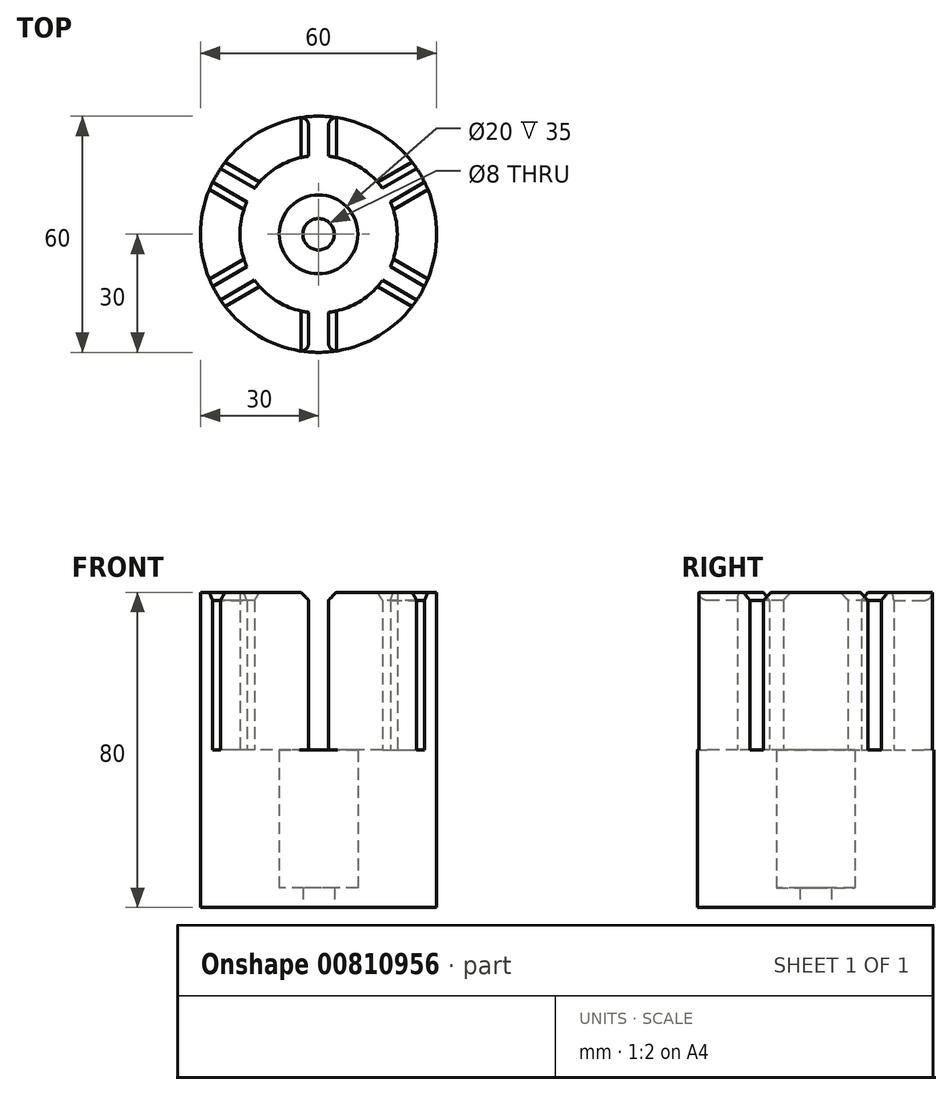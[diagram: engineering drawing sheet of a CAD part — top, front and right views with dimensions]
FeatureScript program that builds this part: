
annotation { "Feature Type Name" : "Feature", "Feature Type Description" : "" }
export const myFeature = defineFeature(function(context is Context, id is Id, definition is map)
    precondition{}
    {
        {
            var Q0;
            Q0=qCreatedBy(makeId("Top.planeOp"),FACE);
            var sketch = newSketch(context, id + "F0", { "sketchPlane" : qUnion([Q0])});
            skCircle(sketch, "E0", {"center": v(0, 0) * mm, "radius": 30 * mm});
            skCircle(sketch, "E1", {"center": v(0, 0) * mm, "radius": 20 * mm});
            skCircle(sketch, "E2", {"center": v(0, 0) * mm, "radius": 10 * mm});
            skCircle(sketch, "E3", {"center": v(0, 0) * mm, "radius": 4 * mm});
            skLineSegment(sketch, "E4", {"start": v(0, 0) * mm, "end": v(0, 30) * mm, "construction": true});
            skLineSegment(sketch, "E5.0", {"start": v(2, 19.9) * mm, "end": v(2, 29.93) * mm, "construction": true});
            skLineSegment(sketch, "E6.0", {"start": v(-2, 19.9) * mm, "end": v(-2, 29.93) * mm, "construction": true});
            skLineSegment(sketch, "E7.1.0", {"start": v(-16.23, 11.68) * mm, "end": v(-24.92, 16.7) * mm});
            skLineSegment(sketch, "E7.1.1", {"start": v(-18.23, 8.22) * mm, "end": v(-26.92, 13.23) * mm});
            skLineSegment(sketch, "E7.2.0", {"start": v(-18.23, -8.22) * mm, "end": v(-26.92, -13.23) * mm});
            skLineSegment(sketch, "E7.2.1", {"start": v(-16.23, -11.68) * mm, "end": v(-24.92, -16.7) * mm});
            skLineSegment(sketch, "E7.3.0", {"start": v(-2, -19.9) * mm, "end": v(-2, -29.93) * mm, "construction": true});
            skLineSegment(sketch, "E7.3.1", {"start": v(2, -19.9) * mm, "end": v(2, -29.93) * mm, "construction": true});
            skLineSegment(sketch, "E7.4.0", {"start": v(16.23, -11.68) * mm, "end": v(24.92, -16.7) * mm});
            skLineSegment(sketch, "E7.4.1", {"start": v(18.23, -8.22) * mm, "end": v(26.92, -13.23) * mm});
            skLineSegment(sketch, "E7.5.0", {"start": v(18.23, 8.22) * mm, "end": v(26.92, 13.23) * mm});
            skLineSegment(sketch, "E7.5.1", {"start": v(16.23, 11.68) * mm, "end": v(24.92, 16.7) * mm});
            skLineSegment(sketch, "E8.0", {"start": v(2.5, 19.84) * mm, "end": v(2.5, 29.9) * mm});
            skLineSegment(sketch, "E9.0", {"start": v(-2.5, 19.84) * mm, "end": v(-2.5, 29.9) * mm});
            skLineSegment(sketch, "E10.1.0", {"start": v(2.5, -19.84) * mm, "end": v(2.5, -29.9) * mm});
            skLineSegment(sketch, "E10.1.1", {"start": v(-2.5, -19.84) * mm, "end": v(-2.5, -29.9) * mm});
            skSolve(sketch);
        }
        {
            var Q0;
            {var subQ0=sQuery(id+"F0.wireOp",EDGE,"E6.0");Q0=makeQuery(id+"F0.imprint","IMPRINT",FACE,{"disambiguationData":[TD([[makeQuery(id+"F0.imprint","IMPRINT",EDGE,{"derivedFrom":subQ0}),1.0]])]});}
            var Q1;
            {var subQ0=sQuery(id+"F0.wireOp",EDGE,"E5.0");Q1=makeQuery(id+"F0.imprint","IMPRINT",FACE,{"disambiguationData":[TD([[makeQuery(id+"F0.imprint","IMPRINT",EDGE,{"derivedFrom":subQ0}),-1.0]])]});}
            var Q2;
            {var subQ0=sQuery(id+"F0.wireOp",EDGE,"E7.4.1");Q2=makeQuery(id+"F0.imprint","IMPRINT",FACE,{"disambiguationData":[TD([[makeQuery(id+"F0.imprint","IMPRINT",EDGE,{"derivedFrom":subQ0}),1.0]])]});}
            var Q3;
            {var subQ0=sQuery(id+"F0.wireOp",EDGE,"E7.3.1");Q3=makeQuery(id+"F0.imprint","IMPRINT",FACE,{"disambiguationData":[TD([[makeQuery(id+"F0.imprint","IMPRINT",EDGE,{"derivedFrom":subQ0}),1.0]])]});}
            var Q4;
            {var subQ0=sQuery(id+"F0.wireOp",EDGE,"E7.2.1");Q4=makeQuery(id+"F0.imprint","IMPRINT",FACE,{"disambiguationData":[TD([[makeQuery(id+"F0.imprint","IMPRINT",EDGE,{"derivedFrom":subQ0}),1.0]])]});}
            var Q5;
            {var subQ0=sQuery(id+"F0.wireOp",EDGE,"E7.1.1");Q5=makeQuery(id+"F0.imprint","IMPRINT",FACE,{"disambiguationData":[TD([[makeQuery(id+"F0.imprint","IMPRINT",EDGE,{"derivedFrom":subQ0}),1.0]])]});}
            var Q6;
            {var subQ0=sQuery(id+"F0.wireOp",EDGE,"E7.5.1");Q6=makeQuery(id+"F0.imprint","IMPRINT",FACE,{"disambiguationData":[TD([[makeQuery(id+"F0.imprint","IMPRINT",EDGE,{"derivedFrom":subQ0}),1.0]])]});}
            var Q7;
            {var subQ0=sQuery(id+"F0.wireOp",EDGE,"E7.1.0");Q7=makeQuery(id+"F0.imprint","IMPRINT",FACE,{"disambiguationData":[TD([[makeQuery(id+"F0.imprint","IMPRINT",EDGE,{"derivedFrom":subQ0}),-1.0]])]});}
            var Q8;
            {var subQ0=sQuery(id+"F0.wireOp",EDGE,"E7.4.0");Q8=makeQuery(id+"F0.imprint","IMPRINT",FACE,{"disambiguationData":[TD([[makeQuery(id+"F0.imprint","IMPRINT",EDGE,{"derivedFrom":subQ0}),-1.0]])]});}
            extrude(context, id + "F1", {"entities" : qUnion([Q0, Q1, Q2, Q3, Q4, Q5, Q6, Q7, Q8]), "depth" : 80 * mm, "offsetDistance" : 25 * mm});
        }
        {
            var Q0;
            {var subQ1=sQuery(id+"F0.wireOp",EDGE,"E0");var subQ3=sQuery(id+"F0.wireOp",EDGE,"e83182f0-5e85-4521-9e30-7dfaf371b3c8.0");var subQ4=makeQuery(id+"F0.imprint","INTERSECT",VERTEX,{"disambiguationData":[OD(0.0)],"derivedFrom":[subQ1,subQ3]});Q0=makeQuery(id+"F0.imprint","IMPRINT",FACE,{"disambiguationData":[TD([[makeQuery(id+"F0.imprint","IMPRINT",EDGE,{"disambiguationData":[TD([[subQ4,-1.0]])],"derivedFrom":subQ3}),-1.0]])]});}
            var Q1;
            {var subQ0=sQuery(id+"F0.wireOp",EDGE,"e83182f0-5e85-4521-9e30-7dfaf371b3c8.0");var subQ1=sQuery(id+"F0.wireOp",EDGE,"E1");var subQ2=makeQuery(id+"F0.imprint","INTERSECT",VERTEX,{"disambiguationData":[OD(0.0)],"derivedFrom":[subQ1,subQ0]});Q1=makeQuery(id+"F0.imprint","IMPRINT",FACE,{"disambiguationData":[TD([[makeQuery(id+"F0.imprint","IMPRINT",EDGE,{"disambiguationData":[TD([[subQ2,-1.0]])],"derivedFrom":subQ1}),-1.0]])]});}
            var Q2;
            {var subQ0=sQuery(id+"F0.wireOp",EDGE,"P4bpMAqq-KJD3-qAAX-vysr-vfVY1KHInT53");var subQ5=sQuery(id+"F0.wireOp",EDGE,"E1");var subQ6=makeQuery(id+"F0.imprint","INTERSECT",VERTEX,{"disambiguationData":[OD(0.0)],"derivedFrom":[subQ5,subQ0]});Q2=makeQuery(id+"F0.imprint","IMPRINT",FACE,{"disambiguationData":[TD([[makeQuery(id+"F0.imprint","IMPRINT",EDGE,{"disambiguationData":[TD([[subQ6,-1.0]])],"derivedFrom":subQ5}),-1.0]])]});}
            var Q3;
            {var subQ0=sQuery(id+"F0.wireOp",EDGE,"sUTsB1f0-u5QJ-SPws-E5oo-vF6zbFCuQsgK");var subQ1=sQuery(id+"F0.wireOp",EDGE,"E0");var subQ2=makeQuery(id+"F0.imprint","INTERSECT",VERTEX,{"derivedFrom":[subQ1,subQ0]});Q3=makeQuery(id+"F0.imprint","IMPRINT",FACE,{"disambiguationData":[TD([[makeQuery(id+"F0.imprint","IMPRINT",EDGE,{"disambiguationData":[TD([[subQ2,1.0]])],"derivedFrom":subQ1}),1.0]])]});}
            var Q4;
            {var subQ0=sQuery(id+"F0.wireOp",EDGE,"sUTsB1f0-u5QJ-SPws-E5oo-vF6zbFCuQsgK");var subQ1=sQuery(id+"F0.wireOp",EDGE,"E0");var subQ2=makeQuery(id+"F0.imprint","INTERSECT",VERTEX,{"derivedFrom":[subQ1,subQ0]});Q4=makeQuery(id+"F0.imprint","IMPRINT",FACE,{"disambiguationData":[TD([[makeQuery(id+"F0.imprint","IMPRINT",EDGE,{"disambiguationData":[TD([[subQ2,-1.0]])],"derivedFrom":subQ1}),1.0]])]});}
            var Q5;
            {var subQ0=sQuery(id+"F0.wireOp",EDGE,"sUTsB1f0-u5QJ-SPws-E5oo-vF6zbFCuQsgK");var subQ1=sQuery(id+"F0.wireOp",EDGE,"E1");var subQ2=makeQuery(id+"F0.imprint","INTERSECT",VERTEX,{"derivedFrom":[subQ1,subQ0]});Q5=makeQuery(id+"F0.imprint","IMPRINT",FACE,{"disambiguationData":[TD([[makeQuery(id+"F0.imprint","IMPRINT",EDGE,{"disambiguationData":[TD([[subQ2,-1.0]])],"derivedFrom":subQ1}),1.0]])]});}
            var Q6;
            {var subQ0=sQuery(id+"F0.wireOp",EDGE,"f20304fd-419b-4c3a-9549-57e4f3b4490c.0");var subQ1=sQuery(id+"F0.wireOp",EDGE,"E1");var subQ2=makeQuery(id+"F0.imprint","INTERSECT",VERTEX,{"derivedFrom":[subQ1,subQ0]});Q6=makeQuery(id+"F0.imprint","IMPRINT",FACE,{"disambiguationData":[TD([[makeQuery(id+"F0.imprint","IMPRINT",EDGE,{"disambiguationData":[TD([[subQ2,-1.0]])],"derivedFrom":subQ1}),1.0]])]});}
            var Q7;
            {var subQ0=sQuery(id+"F0.wireOp",EDGE,"e2eefb9c-702c-4c7c-ab6b-215cc02c1ddd.0");var subQ1=sQuery(id+"F0.wireOp",EDGE,"E1");var subQ2=makeQuery(id+"F0.imprint","INTERSECT",VERTEX,{"disambiguationData":[OD(0.0)],"derivedFrom":[subQ1,subQ0]});Q7=makeQuery(id+"F0.imprint","IMPRINT",FACE,{"disambiguationData":[TD([[makeQuery(id+"F0.imprint","IMPRINT",EDGE,{"disambiguationData":[TD([[subQ2,-1.0]])],"derivedFrom":subQ1}),1.0]])]});}
            var Q8;
            {var subQ0=sQuery(id+"F0.wireOp",EDGE,"P4bpMAqq-KJD3-qAAX-vysr-vfVY1KHInT53");var subQ1=sQuery(id+"F0.wireOp",EDGE,"E1");var subQ2=makeQuery(id+"F0.imprint","INTERSECT",VERTEX,{"disambiguationData":[OD(0.0)],"derivedFrom":[subQ1,subQ0]});Q8=makeQuery(id+"F0.imprint","IMPRINT",FACE,{"disambiguationData":[TD([[makeQuery(id+"F0.imprint","IMPRINT",EDGE,{"disambiguationData":[TD([[subQ2,-1.0]])],"derivedFrom":subQ1}),1.0]])]});}
            var Q9;
            {var subQ0=sQuery(id+"F0.wireOp",EDGE,"e83182f0-5e85-4521-9e30-7dfaf371b3c8.0");var subQ1=sQuery(id+"F0.wireOp",EDGE,"E1");var subQ2=makeQuery(id+"F0.imprint","INTERSECT",VERTEX,{"disambiguationData":[OD(0.0)],"derivedFrom":[subQ1,subQ0]});Q9=makeQuery(id+"F0.imprint","IMPRINT",FACE,{"disambiguationData":[TD([[makeQuery(id+"F0.imprint","IMPRINT",EDGE,{"disambiguationData":[TD([[subQ2,-1.0]])],"derivedFrom":subQ1}),1.0]])]});}
            var Q10;
            {var subQ0=sQuery(id+"F0.wireOp",EDGE,"212b0afc-c16e-482f-bd50-61eb11688d9b.0");var subQ1=sQuery(id+"F0.wireOp",EDGE,"E1");var subQ2=makeQuery(id+"F0.imprint","INTERSECT",VERTEX,{"derivedFrom":[subQ1,subQ0]});Q10=makeQuery(id+"F0.imprint","IMPRINT",FACE,{"disambiguationData":[TD([[makeQuery(id+"F0.imprint","IMPRINT",EDGE,{"disambiguationData":[TD([[subQ2,-1.0]])],"derivedFrom":subQ1}),1.0]])]});}
            var Q11;
            {var subQ0=sQuery(id+"F0.wireOp",EDGE,"EAwv0bRp-eTHg-rzdB-x4oI-au5AC0RZvLWq");var subQ1=sQuery(id+"F0.wireOp",EDGE,"E1");var subQ2=makeQuery(id+"F0.imprint","INTERSECT",VERTEX,{"derivedFrom":[subQ1,subQ0]});Q11=makeQuery(id+"F0.imprint","IMPRINT",FACE,{"disambiguationData":[TD([[makeQuery(id+"F0.imprint","IMPRINT",EDGE,{"disambiguationData":[TD([[subQ2,-1.0]])],"derivedFrom":subQ1}),1.0]])]});}
            var Q12;
            {var subQ0=sQuery(id+"F0.wireOp",EDGE,"EAwv0bRp-eTHg-rzdB-x4oI-au5AC0RZvLWq");var subQ1=sQuery(id+"F0.wireOp",EDGE,"E1");var subQ2=makeQuery(id+"F0.imprint","INTERSECT",VERTEX,{"derivedFrom":[subQ1,subQ0]});Q12=makeQuery(id+"F0.imprint","IMPRINT",FACE,{"disambiguationData":[TD([[makeQuery(id+"F0.imprint","IMPRINT",EDGE,{"disambiguationData":[TD([[subQ2,1.0]])],"derivedFrom":subQ1}),1.0]])]});}
            var Q13;
            {var subQ0=sQuery(id+"F0.wireOp",EDGE,"EAwv0bRp-eTHg-rzdB-x4oI-au5AC0RZvLWq");var subQ1=sQuery(id+"F0.wireOp",EDGE,"E1");var subQ2=makeQuery(id+"F0.imprint","INTERSECT",VERTEX,{"derivedFrom":[subQ1,subQ0]});Q13=makeQuery(id+"F0.imprint","IMPRINT",FACE,{"disambiguationData":[TD([[makeQuery(id+"F0.imprint","IMPRINT",EDGE,{"disambiguationData":[TD([[subQ2,1.0]])],"derivedFrom":subQ1}),-1.0]])]});}
            var Q14;
            {var subQ0=sQuery(id+"F0.wireOp",EDGE,"EAwv0bRp-eTHg-rzdB-x4oI-au5AC0RZvLWq");var subQ1=sQuery(id+"F0.wireOp",EDGE,"E1");var subQ2=makeQuery(id+"F0.imprint","INTERSECT",VERTEX,{"derivedFrom":[subQ1,subQ0]});Q14=makeQuery(id+"F0.imprint","IMPRINT",FACE,{"disambiguationData":[TD([[makeQuery(id+"F0.imprint","IMPRINT",EDGE,{"disambiguationData":[TD([[subQ2,-1.0]])],"derivedFrom":subQ1}),-1.0]])]});}
            var Q15;
            {var subQ1=sQuery(id+"F0.wireOp",EDGE,"E0");var subQ3=sQuery(id+"F0.wireOp",EDGE,"212b0afc-c16e-482f-bd50-61eb11688d9b.0");var subQ4=makeQuery(id+"F0.imprint","INTERSECT",VERTEX,{"derivedFrom":[subQ1,subQ3]});Q15=makeQuery(id+"F0.imprint","IMPRINT",FACE,{"disambiguationData":[TD([[makeQuery(id+"F0.imprint","IMPRINT",EDGE,{"disambiguationData":[TD([[subQ4,1.0]])],"derivedFrom":subQ3}),-1.0]])]});}
            var Q16;
            {var subQ1=sQuery(id+"F0.wireOp",EDGE,"E0");var subQ3=sQuery(id+"F0.wireOp",EDGE,"570f9a7a-61c9-46b9-88a6-6a3669e4d9da.0");var subQ4=makeQuery(id+"F0.imprint","INTERSECT",VERTEX,{"derivedFrom":[subQ1,subQ3]});Q16=makeQuery(id+"F0.imprint","IMPRINT",FACE,{"disambiguationData":[TD([[makeQuery(id+"F0.imprint","IMPRINT",EDGE,{"disambiguationData":[TD([[subQ4,1.0]])],"derivedFrom":subQ3}),1.0]])]});}
            var Q17;
            {var subQ0=sQuery(id+"F0.wireOp",EDGE,"570f9a7a-61c9-46b9-88a6-6a3669e4d9da.0");var subQ1=sQuery(id+"F0.wireOp",EDGE,"E1");var subQ2=makeQuery(id+"F0.imprint","INTERSECT",VERTEX,{"derivedFrom":[subQ1,subQ0]});Q17=makeQuery(id+"F0.imprint","IMPRINT",FACE,{"disambiguationData":[TD([[makeQuery(id+"F0.imprint","IMPRINT",EDGE,{"disambiguationData":[TD([[subQ2,1.0]])],"derivedFrom":subQ1}),1.0]])]});}
            var Q18;
            {var subQ0=sQuery(id+"F0.wireOp",EDGE,"qPpyAoBU-KGxA-Omqg-IoGc-uDFyihY7jVaz");var subQ1=sQuery(id+"F0.wireOp",EDGE,"E1");var subQ2=makeQuery(id+"F0.imprint","INTERSECT",VERTEX,{"derivedFrom":[subQ1,subQ0]});Q18=makeQuery(id+"F0.imprint","IMPRINT",FACE,{"disambiguationData":[TD([[makeQuery(id+"F0.imprint","IMPRINT",EDGE,{"disambiguationData":[TD([[subQ2,-1.0]])],"derivedFrom":subQ1}),1.0]])]});}
            var Q19;
            {var subQ0=sQuery(id+"F0.wireOp",EDGE,"d342ad4c-4ad7-432f-8baf-1a39dd8a6b68.1");var subQ1=sQuery(id+"F0.wireOp",EDGE,"E1");var subQ2=makeQuery(id+"F0.imprint","INTERSECT",VERTEX,{"derivedFrom":[subQ1,subQ0]});Q19=makeQuery(id+"F0.imprint","IMPRINT",FACE,{"disambiguationData":[TD([[makeQuery(id+"F0.imprint","IMPRINT",EDGE,{"disambiguationData":[TD([[subQ2,-1.0]])],"derivedFrom":subQ1}),1.0]])]});}
            var Q20;
            {var subQ0=sQuery(id+"F0.wireOp",EDGE,"d342ad4c-4ad7-432f-8baf-1a39dd8a6b68.1");var subQ1=sQuery(id+"F0.wireOp",EDGE,"E1");var subQ2=makeQuery(id+"F0.imprint","INTERSECT",VERTEX,{"derivedFrom":[subQ1,subQ0]});Q20=makeQuery(id+"F0.imprint","IMPRINT",FACE,{"disambiguationData":[TD([[makeQuery(id+"F0.imprint","IMPRINT",EDGE,{"disambiguationData":[TD([[subQ2,-1.0]])],"derivedFrom":subQ1}),-1.0]])]});}
            var Q21;
            {var subQ0=sQuery(id+"F0.wireOp",EDGE,"qPpyAoBU-KGxA-Omqg-IoGc-uDFyihY7jVaz");var subQ1=sQuery(id+"F0.wireOp",EDGE,"E1");var subQ2=makeQuery(id+"F0.imprint","INTERSECT",VERTEX,{"derivedFrom":[subQ1,subQ0]});Q21=makeQuery(id+"F0.imprint","IMPRINT",FACE,{"disambiguationData":[TD([[makeQuery(id+"F0.imprint","IMPRINT",EDGE,{"disambiguationData":[TD([[subQ2,-1.0]])],"derivedFrom":subQ1}),-1.0]])]});}
            var Q22;
            {var subQ1=sQuery(id+"F0.wireOp",EDGE,"E0");var subQ3=sQuery(id+"F0.wireOp",EDGE,"d342ad4c-4ad7-432f-8baf-1a39dd8a6b68.1");var subQ4=makeQuery(id+"F0.imprint","INTERSECT",VERTEX,{"derivedFrom":[subQ1,subQ3]});Q22=makeQuery(id+"F0.imprint","IMPRINT",FACE,{"disambiguationData":[TD([[makeQuery(id+"F0.imprint","IMPRINT",EDGE,{"disambiguationData":[TD([[subQ4,-1.0]])],"derivedFrom":subQ3}),-1.0]])]});}
            var Q23;
            {var subQ1=sQuery(id+"F0.wireOp",EDGE,"E0");var subQ3=sQuery(id+"F0.wireOp",EDGE,"f20304fd-419b-4c3a-9549-57e4f3b4490c.1");var subQ4=makeQuery(id+"F0.imprint","INTERSECT",VERTEX,{"derivedFrom":[subQ1,subQ3]});Q23=makeQuery(id+"F0.imprint","IMPRINT",FACE,{"disambiguationData":[TD([[makeQuery(id+"F0.imprint","IMPRINT",EDGE,{"disambiguationData":[TD([[subQ4,-1.0]])],"derivedFrom":subQ3}),1.0]])]});}
            var Q24;
            {var subQ0=sQuery(id+"F0.wireOp",EDGE,"e83182f0-5e85-4521-9e30-7dfaf371b3c8.0");var subQ1=sQuery(id+"F0.wireOp",EDGE,"E1");var subQ2=makeQuery(id+"F0.imprint","INTERSECT",VERTEX,{"disambiguationData":[OD(1.0)],"derivedFrom":[subQ1,subQ0]});Q24=makeQuery(id+"F0.imprint","IMPRINT",FACE,{"disambiguationData":[TD([[makeQuery(id+"F0.imprint","IMPRINT",EDGE,{"disambiguationData":[TD([[subQ2,-1.0]])],"derivedFrom":subQ1}),1.0]])]});}
            var Q25;
            {var subQ0=sQuery(id+"F0.wireOp",EDGE,"P4bpMAqq-KJD3-qAAX-vysr-vfVY1KHInT53");var subQ1=sQuery(id+"F0.wireOp",EDGE,"E1");var subQ2=makeQuery(id+"F0.imprint","INTERSECT",VERTEX,{"disambiguationData":[OD(1.0)],"derivedFrom":[subQ1,subQ0]});Q25=makeQuery(id+"F0.imprint","IMPRINT",FACE,{"disambiguationData":[TD([[makeQuery(id+"F0.imprint","IMPRINT",EDGE,{"disambiguationData":[TD([[subQ2,-1.0]])],"derivedFrom":subQ1}),1.0]])]});}
            var Q26;
            {var subQ0=sQuery(id+"F0.wireOp",EDGE,"e2eefb9c-702c-4c7c-ab6b-215cc02c1ddd.0");var subQ1=sQuery(id+"F0.wireOp",EDGE,"E1");var subQ2=makeQuery(id+"F0.imprint","INTERSECT",VERTEX,{"disambiguationData":[OD(1.0)],"derivedFrom":[subQ1,subQ0]});Q26=makeQuery(id+"F0.imprint","IMPRINT",FACE,{"disambiguationData":[TD([[makeQuery(id+"F0.imprint","IMPRINT",EDGE,{"disambiguationData":[TD([[subQ2,-1.0]])],"derivedFrom":subQ1}),1.0]])]});}
            var Q27;
            {var subQ3=sQuery(id+"F0.wireOp",EDGE,"e2eefb9c-702c-4c7c-ab6b-215cc02c1ddd.0");var subQ5=sQuery(id+"F0.wireOp",EDGE,"E1");var subQ6=makeQuery(id+"F0.imprint","INTERSECT",VERTEX,{"disambiguationData":[OD(1.0)],"derivedFrom":[subQ5,subQ3]});Q27=makeQuery(id+"F0.imprint","IMPRINT",FACE,{"disambiguationData":[TD([[makeQuery(id+"F0.imprint","IMPRINT",EDGE,{"disambiguationData":[TD([[subQ6,-1.0]])],"derivedFrom":subQ5}),-1.0]])]});}
            var Q28;
            {var subQ0=sQuery(id+"F0.wireOp",EDGE,"P4bpMAqq-KJD3-qAAX-vysr-vfVY1KHInT53");var subQ1=sQuery(id+"F0.wireOp",EDGE,"E1");var subQ2=makeQuery(id+"F0.imprint","INTERSECT",VERTEX,{"disambiguationData":[OD(1.0)],"derivedFrom":[subQ1,subQ0]});Q28=makeQuery(id+"F0.imprint","IMPRINT",FACE,{"disambiguationData":[TD([[makeQuery(id+"F0.imprint","IMPRINT",EDGE,{"disambiguationData":[TD([[subQ2,-1.0]])],"derivedFrom":subQ1}),-1.0]])]});}
            var Q29;
            {var subQ1=sQuery(id+"F0.wireOp",EDGE,"E0");var subQ3=sQuery(id+"F0.wireOp",EDGE,"e83182f0-5e85-4521-9e30-7dfaf371b3c8.0");var subQ4=makeQuery(id+"F0.imprint","INTERSECT",VERTEX,{"disambiguationData":[OD(1.0)],"derivedFrom":[subQ1,subQ3]});Q29=makeQuery(id+"F0.imprint","IMPRINT",FACE,{"disambiguationData":[TD([[makeQuery(id+"F0.imprint","IMPRINT",EDGE,{"disambiguationData":[TD([[subQ4,1.0]])],"derivedFrom":subQ3}),-1.0]])]});}
            var Q30;
            {var subQ0=sQuery(id+"F0.wireOp",EDGE,"570f9a7a-61c9-46b9-88a6-6a3669e4d9da.1");var subQ1=sQuery(id+"F0.wireOp",EDGE,"E1");var subQ2=makeQuery(id+"F0.imprint","INTERSECT",VERTEX,{"derivedFrom":[subQ1,subQ0]});Q30=makeQuery(id+"F0.imprint","IMPRINT",FACE,{"disambiguationData":[TD([[makeQuery(id+"F0.imprint","IMPRINT",EDGE,{"disambiguationData":[TD([[subQ2,-1.0]])],"derivedFrom":subQ1}),1.0]])]});}
            var Q31;
            {var subQ0=sQuery(id+"F0.wireOp",EDGE,"Xt3IS3Tl-rmhy-tMjK-yUDQ-kadHyxG95FHM");var subQ1=sQuery(id+"F0.wireOp",EDGE,"E1");var subQ2=makeQuery(id+"F0.imprint","INTERSECT",VERTEX,{"derivedFrom":[subQ1,subQ0]});Q31=makeQuery(id+"F0.imprint","IMPRINT",FACE,{"disambiguationData":[TD([[makeQuery(id+"F0.imprint","IMPRINT",EDGE,{"disambiguationData":[TD([[subQ2,-1.0]])],"derivedFrom":subQ1}),1.0]])]});}
            var Q32;
            {var subQ0=sQuery(id+"F0.wireOp",EDGE,"Xt3IS3Tl-rmhy-tMjK-yUDQ-kadHyxG95FHM");var subQ1=sQuery(id+"F0.wireOp",EDGE,"E0");var subQ2=makeQuery(id+"F0.imprint","INTERSECT",VERTEX,{"derivedFrom":[subQ1,subQ0]});Q32=makeQuery(id+"F0.imprint","IMPRINT",FACE,{"disambiguationData":[TD([[makeQuery(id+"F0.imprint","IMPRINT",EDGE,{"disambiguationData":[TD([[subQ2,1.0]])],"derivedFrom":subQ1}),1.0]])]});}
            var Q33;
            {var subQ0=sQuery(id+"F0.wireOp",EDGE,"Xt3IS3Tl-rmhy-tMjK-yUDQ-kadHyxG95FHM");var subQ1=sQuery(id+"F0.wireOp",EDGE,"E0");var subQ2=makeQuery(id+"F0.imprint","INTERSECT",VERTEX,{"derivedFrom":[subQ1,subQ0]});Q33=makeQuery(id+"F0.imprint","IMPRINT",FACE,{"disambiguationData":[TD([[makeQuery(id+"F0.imprint","IMPRINT",EDGE,{"disambiguationData":[TD([[subQ2,-1.0]])],"derivedFrom":subQ1}),1.0]])]});}
            var Q34;
            {var subQ0=sQuery(id+"F0.wireOp",EDGE,"212b0afc-c16e-482f-bd50-61eb11688d9b.1");var subQ1=sQuery(id+"F0.wireOp",EDGE,"E1");var subQ2=makeQuery(id+"F0.imprint","INTERSECT",VERTEX,{"derivedFrom":[subQ1,subQ0]});Q34=makeQuery(id+"F0.imprint","IMPRINT",FACE,{"disambiguationData":[TD([[makeQuery(id+"F0.imprint","IMPRINT",EDGE,{"disambiguationData":[TD([[subQ2,-1.0]])],"derivedFrom":subQ1}),1.0]])]});}
            var Q35;
            {var subQ0=sQuery(id+"F0.wireOp",EDGE,"d342ad4c-4ad7-432f-8baf-1a39dd8a6b68.0");var subQ1=sQuery(id+"F0.wireOp",EDGE,"E1");var subQ2=makeQuery(id+"F0.imprint","INTERSECT",VERTEX,{"derivedFrom":[subQ1,subQ0]});Q35=makeQuery(id+"F0.imprint","IMPRINT",FACE,{"disambiguationData":[TD([[makeQuery(id+"F0.imprint","IMPRINT",EDGE,{"disambiguationData":[TD([[subQ2,-1.0]])],"derivedFrom":subQ1}),1.0]])]});}
            extrude(context, id + "F2", {"entities" : qUnion([Q0, Q1, Q2, Q3, Q4, Q5, Q6, Q7, Q8, Q9, Q10, Q11, Q12, Q13, Q14, Q15, Q16, Q17, Q18, Q19, Q20, Q21, Q22, Q23, Q24, Q25, Q26, Q27, Q28, Q29, Q30, Q31, Q32, Q33, Q34, Q35]), "operationType" : NewBodyOperationType.ADD, "depth" : 40 * mm, "offsetDistance" : 25 * mm});
        }
        {
            var Q0;
            {var subQ0=sQuery(id+"F0.wireOp",EDGE,"d342ad4c-4ad7-432f-8baf-1a39dd8a6b68.0");var subQ1=sQuery(id+"F0.wireOp",EDGE,"E2");var subQ2=makeQuery(id+"F0.imprint","INTERSECT",VERTEX,{"derivedFrom":[subQ1,subQ0]});Q0=makeQuery(id+"F0.imprint","IMPRINT",FACE,{"disambiguationData":[TD([[makeQuery(id+"F0.imprint","IMPRINT",EDGE,{"disambiguationData":[TD([[subQ2,-1.0]])],"derivedFrom":subQ1}),1.0]])]});}
            var Q1;
            {var subQ0=sQuery(id+"F0.wireOp",EDGE,"sUTsB1f0-u5QJ-SPws-E5oo-vF6zbFCuQsgK");var subQ1=sQuery(id+"F0.wireOp",EDGE,"E2");var subQ2=makeQuery(id+"F0.imprint","INTERSECT",VERTEX,{"derivedFrom":[subQ1,subQ0]});Q1=makeQuery(id+"F0.imprint","IMPRINT",FACE,{"disambiguationData":[TD([[makeQuery(id+"F0.imprint","IMPRINT",EDGE,{"disambiguationData":[TD([[subQ2,-1.0]])],"derivedFrom":subQ1}),1.0]])]});}
            var Q2;
            {var subQ3=sQuery(id+"F0.wireOp",EDGE,"e2eefb9c-702c-4c7c-ab6b-215cc02c1ddd.0");var subQ6=sQuery(id+"F0.wireOp",EDGE,"E3");var subQ7=makeQuery(id+"F0.imprint","INTERSECT",VERTEX,{"disambiguationData":[OD(0.0)],"derivedFrom":[subQ6,subQ3]});Q2=makeQuery(id+"F0.imprint","IMPRINT",FACE,{"disambiguationData":[TD([[makeQuery(id+"F0.imprint","IMPRINT",EDGE,{"disambiguationData":[TD([[subQ7,-1.0]])],"derivedFrom":subQ6}),-1.0]])]});}
            var Q3;
            {var subQ0=sQuery(id+"F0.wireOp",EDGE,"212b0afc-c16e-482f-bd50-61eb11688d9b.1");var subQ1=sQuery(id+"F0.wireOp",EDGE,"E2");var subQ2=makeQuery(id+"F0.imprint","INTERSECT",VERTEX,{"derivedFrom":[subQ1,subQ0]});Q3=makeQuery(id+"F0.imprint","IMPRINT",FACE,{"disambiguationData":[TD([[makeQuery(id+"F0.imprint","IMPRINT",EDGE,{"disambiguationData":[TD([[subQ2,-1.0]])],"derivedFrom":subQ1}),1.0]])]});}
            var Q4;
            {var subQ0=sQuery(id+"F0.wireOp",EDGE,"Xt3IS3Tl-rmhy-tMjK-yUDQ-kadHyxG95FHM");var subQ1=sQuery(id+"F0.wireOp",EDGE,"E2");var subQ2=makeQuery(id+"F0.imprint","INTERSECT",VERTEX,{"derivedFrom":[subQ1,subQ0]});Q4=makeQuery(id+"F0.imprint","IMPRINT",FACE,{"disambiguationData":[TD([[makeQuery(id+"F0.imprint","IMPRINT",EDGE,{"disambiguationData":[TD([[subQ2,-1.0]])],"derivedFrom":subQ1}),1.0]])]});}
            var Q5;
            {var subQ5=sQuery(id+"F0.wireOp",EDGE,"E3");var subQ7=sQuery(id+"F0.wireOp",EDGE,"d342ad4c-4ad7-432f-8baf-1a39dd8a6b68.0");var subQ8=makeQuery(id+"F0.imprint","INTERSECT",VERTEX,{"derivedFrom":[subQ5,subQ7]});Q5=makeQuery(id+"F0.imprint","IMPRINT",FACE,{"disambiguationData":[TD([[makeQuery(id+"F0.imprint","IMPRINT",EDGE,{"disambiguationData":[TD([[subQ8,-1.0]])],"derivedFrom":subQ5}),-1.0]])]});}
            var Q6;
            {var subQ0=sQuery(id+"F0.wireOp",EDGE,"570f9a7a-61c9-46b9-88a6-6a3669e4d9da.1");var subQ1=sQuery(id+"F0.wireOp",EDGE,"E2");var subQ2=makeQuery(id+"F0.imprint","INTERSECT",VERTEX,{"derivedFrom":[subQ1,subQ0]});Q6=makeQuery(id+"F0.imprint","IMPRINT",FACE,{"disambiguationData":[TD([[makeQuery(id+"F0.imprint","IMPRINT",EDGE,{"disambiguationData":[TD([[subQ2,-1.0]])],"derivedFrom":subQ1}),1.0]])]});}
            var Q7;
            {var subQ0=sQuery(id+"F0.wireOp",EDGE,"e2eefb9c-702c-4c7c-ab6b-215cc02c1ddd.0");var subQ1=sQuery(id+"F0.wireOp",EDGE,"E2");var subQ2=makeQuery(id+"F0.imprint","INTERSECT",VERTEX,{"disambiguationData":[OD(1.0)],"derivedFrom":[subQ1,subQ0]});Q7=makeQuery(id+"F0.imprint","IMPRINT",FACE,{"disambiguationData":[TD([[makeQuery(id+"F0.imprint","IMPRINT",EDGE,{"disambiguationData":[TD([[subQ2,-1.0]])],"derivedFrom":subQ1}),1.0]])]});}
            var Q8;
            {var subQ0=sQuery(id+"F0.wireOp",EDGE,"P4bpMAqq-KJD3-qAAX-vysr-vfVY1KHInT53");var subQ1=sQuery(id+"F0.wireOp",EDGE,"E2");var subQ2=makeQuery(id+"F0.imprint","INTERSECT",VERTEX,{"disambiguationData":[OD(1.0)],"derivedFrom":[subQ1,subQ0]});Q8=makeQuery(id+"F0.imprint","IMPRINT",FACE,{"disambiguationData":[TD([[makeQuery(id+"F0.imprint","IMPRINT",EDGE,{"disambiguationData":[TD([[subQ2,-1.0]])],"derivedFrom":subQ1}),1.0]])]});}
            var Q9;
            {var subQ0=sQuery(id+"F0.wireOp",EDGE,"570f9a7a-61c9-46b9-88a6-6a3669e4d9da.1");var subQ1=sQuery(id+"F0.wireOp",EDGE,"E3");var subQ2=makeQuery(id+"F0.imprint","INTERSECT",VERTEX,{"derivedFrom":[subQ1,subQ0]});Q9=makeQuery(id+"F0.imprint","IMPRINT",FACE,{"disambiguationData":[TD([[makeQuery(id+"F0.imprint","IMPRINT",EDGE,{"disambiguationData":[TD([[subQ2,-1.0]])],"derivedFrom":subQ1}),-1.0]])]});}
            var Q10;
            {var subQ0=sQuery(id+"F0.wireOp",EDGE,"e83182f0-5e85-4521-9e30-7dfaf371b3c8.0");var subQ1=sQuery(id+"F0.wireOp",EDGE,"E2");var subQ2=makeQuery(id+"F0.imprint","INTERSECT",VERTEX,{"disambiguationData":[OD(1.0)],"derivedFrom":[subQ1,subQ0]});Q10=makeQuery(id+"F0.imprint","IMPRINT",FACE,{"disambiguationData":[TD([[makeQuery(id+"F0.imprint","IMPRINT",EDGE,{"disambiguationData":[TD([[subQ2,-1.0]])],"derivedFrom":subQ1}),1.0]])]});}
            var Q11;
            {var subQ0=sQuery(id+"F0.wireOp",EDGE,"d342ad4c-4ad7-432f-8baf-1a39dd8a6b68.1");var subQ1=sQuery(id+"F0.wireOp",EDGE,"E2");var subQ2=makeQuery(id+"F0.imprint","INTERSECT",VERTEX,{"derivedFrom":[subQ1,subQ0]});Q11=makeQuery(id+"F0.imprint","IMPRINT",FACE,{"disambiguationData":[TD([[makeQuery(id+"F0.imprint","IMPRINT",EDGE,{"disambiguationData":[TD([[subQ2,-1.0]])],"derivedFrom":subQ1}),1.0]])]});}
            var Q12;
            {var subQ0=sQuery(id+"F0.wireOp",EDGE,"qPpyAoBU-KGxA-Omqg-IoGc-uDFyihY7jVaz");var subQ1=sQuery(id+"F0.wireOp",EDGE,"E2");var subQ2=makeQuery(id+"F0.imprint","INTERSECT",VERTEX,{"derivedFrom":[subQ1,subQ0]});Q12=makeQuery(id+"F0.imprint","IMPRINT",FACE,{"disambiguationData":[TD([[makeQuery(id+"F0.imprint","IMPRINT",EDGE,{"disambiguationData":[TD([[subQ2,-1.0]])],"derivedFrom":subQ1}),1.0]])]});}
            var Q13;
            {var subQ0=sQuery(id+"F0.wireOp",EDGE,"e83182f0-5e85-4521-9e30-7dfaf371b3c8.0");var subQ1=sQuery(id+"F0.wireOp",EDGE,"E3");var subQ2=makeQuery(id+"F0.imprint","INTERSECT",VERTEX,{"disambiguationData":[OD(0.0)],"derivedFrom":[subQ1,subQ0]});Q13=makeQuery(id+"F0.imprint","IMPRINT",FACE,{"disambiguationData":[TD([[makeQuery(id+"F0.imprint","IMPRINT",EDGE,{"disambiguationData":[TD([[subQ2,1.0]])],"derivedFrom":subQ1}),-1.0]])]});}
            var Q14;
            {var subQ0=sQuery(id+"F0.wireOp",EDGE,"570f9a7a-61c9-46b9-88a6-6a3669e4d9da.0");var subQ1=sQuery(id+"F0.wireOp",EDGE,"E2");var subQ2=makeQuery(id+"F0.imprint","INTERSECT",VERTEX,{"derivedFrom":[subQ1,subQ0]});Q14=makeQuery(id+"F0.imprint","IMPRINT",FACE,{"disambiguationData":[TD([[makeQuery(id+"F0.imprint","IMPRINT",EDGE,{"disambiguationData":[TD([[subQ2,1.0]])],"derivedFrom":subQ1}),1.0]])]});}
            var Q15;
            {var subQ0=sQuery(id+"F0.wireOp",EDGE,"EAwv0bRp-eTHg-rzdB-x4oI-au5AC0RZvLWq");var subQ1=sQuery(id+"F0.wireOp",EDGE,"E2");var subQ2=makeQuery(id+"F0.imprint","INTERSECT",VERTEX,{"derivedFrom":[subQ1,subQ0]});Q15=makeQuery(id+"F0.imprint","IMPRINT",FACE,{"disambiguationData":[TD([[makeQuery(id+"F0.imprint","IMPRINT",EDGE,{"disambiguationData":[TD([[subQ2,1.0]])],"derivedFrom":subQ1}),1.0]])]});}
            var Q16;
            {var subQ0=sQuery(id+"F0.wireOp",EDGE,"EAwv0bRp-eTHg-rzdB-x4oI-au5AC0RZvLWq");var subQ1=sQuery(id+"F0.wireOp",EDGE,"E2");var subQ2=makeQuery(id+"F0.imprint","INTERSECT",VERTEX,{"derivedFrom":[subQ1,subQ0]});Q16=makeQuery(id+"F0.imprint","IMPRINT",FACE,{"disambiguationData":[TD([[makeQuery(id+"F0.imprint","IMPRINT",EDGE,{"disambiguationData":[TD([[subQ2,-1.0]])],"derivedFrom":subQ1}),1.0]])]});}
            var Q17;
            {var subQ0=sQuery(id+"F0.wireOp",EDGE,"212b0afc-c16e-482f-bd50-61eb11688d9b.0");var subQ1=sQuery(id+"F0.wireOp",EDGE,"E2");var subQ2=makeQuery(id+"F0.imprint","INTERSECT",VERTEX,{"derivedFrom":[subQ1,subQ0]});Q17=makeQuery(id+"F0.imprint","IMPRINT",FACE,{"disambiguationData":[TD([[makeQuery(id+"F0.imprint","IMPRINT",EDGE,{"disambiguationData":[TD([[subQ2,-1.0]])],"derivedFrom":subQ1}),1.0]])]});}
            var Q18;
            {var subQ0=sQuery(id+"F0.wireOp",EDGE,"e83182f0-5e85-4521-9e30-7dfaf371b3c8.0");var subQ1=sQuery(id+"F0.wireOp",EDGE,"E2");var subQ2=makeQuery(id+"F0.imprint","INTERSECT",VERTEX,{"disambiguationData":[OD(0.0)],"derivedFrom":[subQ1,subQ0]});Q18=makeQuery(id+"F0.imprint","IMPRINT",FACE,{"disambiguationData":[TD([[makeQuery(id+"F0.imprint","IMPRINT",EDGE,{"disambiguationData":[TD([[subQ2,-1.0]])],"derivedFrom":subQ1}),1.0]])]});}
            var Q19;
            {var subQ0=sQuery(id+"F0.wireOp",EDGE,"f20304fd-419b-4c3a-9549-57e4f3b4490c.1");var subQ1=sQuery(id+"F0.wireOp",EDGE,"E3");var subQ2=makeQuery(id+"F0.imprint","INTERSECT",VERTEX,{"derivedFrom":[subQ1,subQ0]});Q19=makeQuery(id+"F0.imprint","IMPRINT",FACE,{"disambiguationData":[TD([[makeQuery(id+"F0.imprint","IMPRINT",EDGE,{"disambiguationData":[TD([[subQ2,-1.0]])],"derivedFrom":subQ1}),-1.0]])]});}
            var Q20;
            {var subQ0=sQuery(id+"F0.wireOp",EDGE,"P4bpMAqq-KJD3-qAAX-vysr-vfVY1KHInT53");var subQ1=sQuery(id+"F0.wireOp",EDGE,"E2");var subQ2=makeQuery(id+"F0.imprint","INTERSECT",VERTEX,{"disambiguationData":[OD(0.0)],"derivedFrom":[subQ1,subQ0]});Q20=makeQuery(id+"F0.imprint","IMPRINT",FACE,{"disambiguationData":[TD([[makeQuery(id+"F0.imprint","IMPRINT",EDGE,{"disambiguationData":[TD([[subQ2,-1.0]])],"derivedFrom":subQ1}),1.0]])]});}
            var Q21;
            {var subQ0=sQuery(id+"F0.wireOp",EDGE,"e2eefb9c-702c-4c7c-ab6b-215cc02c1ddd.0");var subQ1=sQuery(id+"F0.wireOp",EDGE,"E2");var subQ2=makeQuery(id+"F0.imprint","INTERSECT",VERTEX,{"disambiguationData":[OD(0.0)],"derivedFrom":[subQ1,subQ0]});Q21=makeQuery(id+"F0.imprint","IMPRINT",FACE,{"disambiguationData":[TD([[makeQuery(id+"F0.imprint","IMPRINT",EDGE,{"disambiguationData":[TD([[subQ2,-1.0]])],"derivedFrom":subQ1}),1.0]])]});}
            var Q22;
            {var subQ0=sQuery(id+"F0.wireOp",EDGE,"f20304fd-419b-4c3a-9549-57e4f3b4490c.0");var subQ1=sQuery(id+"F0.wireOp",EDGE,"E2");var subQ2=makeQuery(id+"F0.imprint","INTERSECT",VERTEX,{"derivedFrom":[subQ1,subQ0]});Q22=makeQuery(id+"F0.imprint","IMPRINT",FACE,{"disambiguationData":[TD([[makeQuery(id+"F0.imprint","IMPRINT",EDGE,{"disambiguationData":[TD([[subQ2,-1.0]])],"derivedFrom":subQ1}),1.0]])]});}
            var Q23;
            {var subQ0=sQuery(id+"F0.wireOp",EDGE,"212b0afc-c16e-482f-bd50-61eb11688d9b.0");var subQ1=sQuery(id+"F0.wireOp",EDGE,"E3");var subQ2=makeQuery(id+"F0.imprint","INTERSECT",VERTEX,{"derivedFrom":[subQ1,subQ0]});Q23=makeQuery(id+"F0.imprint","IMPRINT",FACE,{"disambiguationData":[TD([[makeQuery(id+"F0.imprint","IMPRINT",EDGE,{"disambiguationData":[TD([[subQ2,-1.0]])],"derivedFrom":subQ1}),-1.0]])]});}
            var Q24;
            {var subQ0=sQuery(id+"F0.wireOp",EDGE,"f20304fd-419b-4c3a-9549-57e4f3b4490c.0");var subQ1=sQuery(id+"F0.wireOp",EDGE,"E3");var subQ2=makeQuery(id+"F0.imprint","INTERSECT",VERTEX,{"disambiguationData":[OD(0.0)],"derivedFrom":[subQ1,subQ0]});Q24=makeQuery(id+"F0.imprint","IMPRINT",FACE,{"disambiguationData":[TD([[makeQuery(id+"F0.imprint","IMPRINT",EDGE,{"disambiguationData":[TD([[subQ2,-1.0]])],"derivedFrom":subQ1}),-1.0]])]});}
            var Q25;
            {var subQ3=sQuery(id+"F0.wireOp",EDGE,"212b0afc-c16e-482f-bd50-61eb11688d9b.1");var subQ5=sQuery(id+"F0.wireOp",EDGE,"E3");var subQ6=makeQuery(id+"F0.imprint","INTERSECT",VERTEX,{"disambiguationData":[OD(0.0)],"derivedFrom":[subQ5,subQ3]});Q25=makeQuery(id+"F0.imprint","IMPRINT",FACE,{"disambiguationData":[TD([[makeQuery(id+"F0.imprint","IMPRINT",EDGE,{"disambiguationData":[TD([[subQ6,-1.0]])],"derivedFrom":subQ5}),-1.0]])]});}
            var Q26;
            {var subQ0=sQuery(id+"F0.wireOp",EDGE,"d342ad4c-4ad7-432f-8baf-1a39dd8a6b68.0");var subQ1=sQuery(id+"F0.wireOp",EDGE,"E3");var subQ2=makeQuery(id+"F0.imprint","INTERSECT",VERTEX,{"disambiguationData":[OD(0.0)],"derivedFrom":[subQ1,subQ0]});Q26=makeQuery(id+"F0.imprint","IMPRINT",FACE,{"disambiguationData":[TD([[makeQuery(id+"F0.imprint","IMPRINT",EDGE,{"disambiguationData":[TD([[subQ2,-1.0]])],"derivedFrom":subQ1}),-1.0]])]});}
            var Q27;
            {var subQ0=sQuery(id+"F0.wireOp",EDGE,"570f9a7a-61c9-46b9-88a6-6a3669e4d9da.1");var subQ1=sQuery(id+"F0.wireOp",EDGE,"E3");var subQ2=makeQuery(id+"F0.imprint","INTERSECT",VERTEX,{"disambiguationData":[OD(0.0)],"derivedFrom":[subQ1,subQ0]});Q27=makeQuery(id+"F0.imprint","IMPRINT",FACE,{"disambiguationData":[TD([[makeQuery(id+"F0.imprint","IMPRINT",EDGE,{"disambiguationData":[TD([[subQ2,-1.0]])],"derivedFrom":subQ1}),-1.0]])]});}
            extrude(context, id + "F3", {"entities" : qUnion([Q0, Q1, Q2, Q3, Q4, Q5, Q6, Q7, Q8, Q9, Q10, Q11, Q12, Q13, Q14, Q15, Q16, Q17, Q18, Q19, Q20, Q21, Q22, Q23, Q24, Q25, Q26, Q27]), "operationType" : NewBodyOperationType.ADD, "depth" : 5 * mm, "offsetDistance" : 25 * mm});
        }
        {
            var Q0;
            Q0=makeQuery(id+"F1.opExtrude","CAP_EDGE",EDGE,{"disambiguationData":[OSD([sQuery(id+"F0.wireOp",EDGE,"E7.1.0")])],"isStart":false});
            var Q1;
            Q1=makeQuery(id+"F1.opExtrude","CAP_EDGE",EDGE,{"disambiguationData":[OSD([sQuery(id+"F0.wireOp",EDGE,"E7.1.1")])],"isStart":false});
            var Q2;
            Q2=makeQuery(id+"F1.opExtrude","CAP_EDGE",EDGE,{"disambiguationData":[OSD([sQuery(id+"F0.wireOp",EDGE,"E7.2.0")])],"isStart":false});
            var Q3;
            Q3=makeQuery(id+"F1.opExtrude","CAP_EDGE",EDGE,{"disambiguationData":[OSD([sQuery(id+"F0.wireOp",EDGE,"E7.2.1")])],"isStart":false});
            var Q4;
            Q4=makeQuery(id+"F1.opExtrude","CAP_EDGE",EDGE,{"disambiguationData":[OSD([sQuery(id+"F0.wireOp",EDGE,"E7.4.0")])],"isStart":false});
            var Q5;
            Q5=makeQuery(id+"F1.opExtrude","CAP_EDGE",EDGE,{"disambiguationData":[OSD([sQuery(id+"F0.wireOp",EDGE,"E7.4.1")])],"isStart":false});
            var Q6;
            Q6=makeQuery(id+"F1.opExtrude","CAP_EDGE",EDGE,{"disambiguationData":[OSD([sQuery(id+"F0.wireOp",EDGE,"E7.5.0")])],"isStart":false});
            var Q7;
            Q7=makeQuery(id+"F1.opExtrude","CAP_EDGE",EDGE,{"disambiguationData":[OSD([sQuery(id+"F0.wireOp",EDGE,"E7.5.1")])],"isStart":false});
            var Q8;
            Q8=makeQuery(id+"F1.opExtrude","CAP_EDGE",EDGE,{"disambiguationData":[OSD([sQuery(id+"F0.wireOp",EDGE,"E9.0")])],"isStart":false});
            var Q9;
            Q9=makeQuery(id+"F1.opExtrude","CAP_EDGE",EDGE,{"disambiguationData":[OSD([sQuery(id+"F0.wireOp",EDGE,"E8.0")])],"isStart":false});
            var Q10;
            Q10=makeQuery(id+"F1.opExtrude","CAP_EDGE",EDGE,{"disambiguationData":[OSD([sQuery(id+"F0.wireOp",EDGE,"E10.1.0")])],"isStart":false});
            var Q11;
            Q11=makeQuery(id+"F1.opExtrude","CAP_EDGE",EDGE,{"disambiguationData":[OSD([sQuery(id+"F0.wireOp",EDGE,"E10.1.1")])],"isStart":false});
            chamfer(context, id + "F4", {"entities" : qUnion([Q0, Q1, Q2, Q3, Q4, Q5, Q6, Q7, Q8, Q9, Q10, Q11]), "width" : 2 * mm, "tangentPropagation" : true});
        }
        {
            var Q0;
            Q0=makeQuery(id+"F1.opExtrude","SWEPT_EDGE",EDGE,{"disambiguationData":[OSD([sQuery(id+"F0.wireOp",EDGE,"E0"),sQuery(id+"F0.wireOp",EDGE,"E9.0")])]});
            var Q1;
            Q1=makeQuery(id+"F1.opExtrude","SWEPT_EDGE",EDGE,{"disambiguationData":[OSD([sQuery(id+"F0.wireOp",EDGE,"E0"),sQuery(id+"F0.wireOp",EDGE,"E8.0")])]});
            var Q2;
            Q2=makeQuery(id+"F1.opExtrude","SWEPT_EDGE",EDGE,{"disambiguationData":[OSD([sQuery(id+"F0.wireOp",EDGE,"E0"),sQuery(id+"F0.wireOp",EDGE,"E10.1.1")])]});
            var Q3;
            Q3=makeQuery(id+"F1.opExtrude","SWEPT_EDGE",EDGE,{"disambiguationData":[OSD([sQuery(id+"F0.wireOp",EDGE,"E0"),sQuery(id+"F0.wireOp",EDGE,"E10.1.0")])]});
            fillet(context, id + "F5", {"entities" : qUnion([Q0, Q1, Q2, Q3]), "radius" : 2 * mm, "tangentPropagation" : true, "allowEdgeOverflow" : false});
        }
    });
